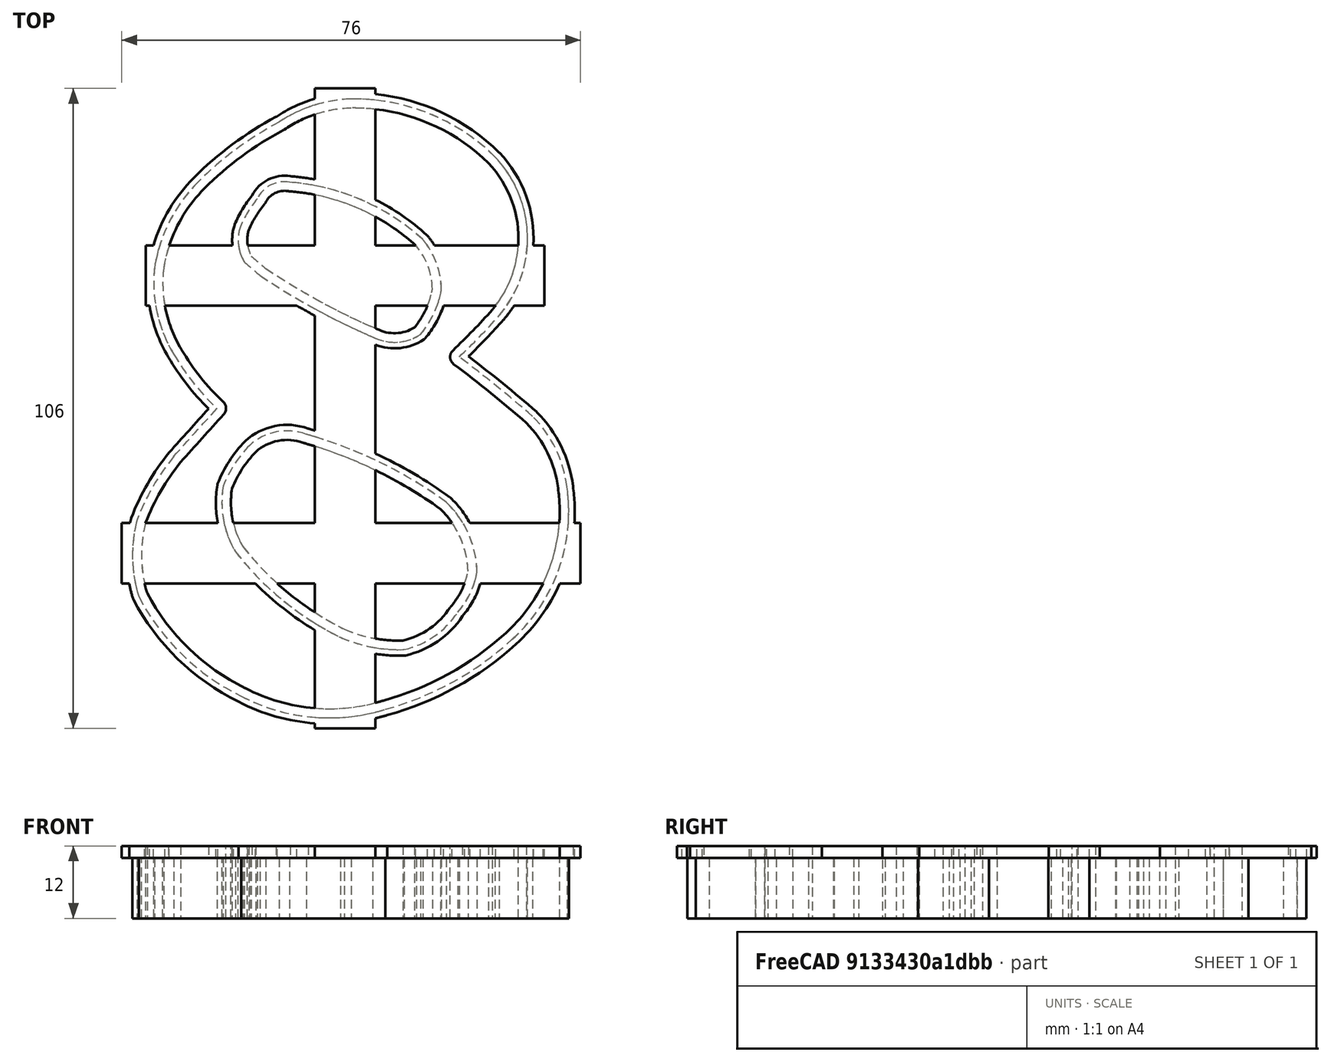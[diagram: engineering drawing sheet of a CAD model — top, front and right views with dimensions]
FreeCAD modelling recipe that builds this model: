
FCSTD DOCUMENT  (FreeCAD 0.20R27319 (Git))
Label: NumberCutter_8
License: All rights reserved
LicenseURL: http://en.wikipedia.org/wiki/All_rights_reserved
objects: Part::Box×3, Part::Offset2D×2, Part::Extrusion×2, Part::MultiFuse×2, Image::ImagePlane×1, Sketcher::SketchObject×1, PartDesign::Body×1
note: 11 computed .brp shape members not serialized (recipe doc carries the construction recipe); baked Part::Feature solids carry a one-line shape summary decoded from their .brp

FEATURE [Image::ImagePlane] ImagePlane
  XSize = 70
  YSize = 100
FEATURE [Sketcher::SketchObject] Sketch
  FullyConstrained = false
  MapMode = 5
  Support = -> [XY_Plane]
  sketch-geometry (35):
    g0: ArcOfCircle CenterX=0.459439 CenterY=17.8982 CenterZ=0 NormalX=0 NormalY=0 NormalZ=1 AngleXU=0 Radius=33.3477 StartAngle=0.793394 EndAngle=1.58457
    g1: ArcOfCircle CenterX=9.51821 CenterY=28.1344 CenterZ=0 NormalX=0 NormalY=0 NormalZ=1 AngleXU=0 Radius=19.7112 StartAngle=5.5764 EndAngle=7.03987
    g2: ArcOfCircle CenterX=-59.3435 CenterY=89.8922 CenterZ=0 NormalX=0 NormalY=0 NormalZ=1 AngleXU=0 Radius=112.205 StartAngle=5.47177 EndAngle=5.55639
    g3: ArcOfCircle CenterX=-125.981 CenterY=-181.648 CenterZ=0 NormalX=0 NormalY=0 NormalZ=1 AngleXU=0 Radius=238.464 StartAngle=0.857411 EndAngle=0.923048
    g4: ArcOfCircle CenterX=15.7711 CenterY=-15.5384 CenterZ=0 NormalX=0 NormalY=0 NormalZ=1 AngleXU=0 Radius=20.1558 StartAngle=0.124366 EndAngle=0.782145
    g5: ArcOfCircle CenterX=7.39522 CenterY=-17.0935 CenterZ=0 NormalX=0 NormalY=0 NormalZ=1 AngleXU=0 Radius=28.6643 StartAngle=5.44901 EndAngle=6.42514
    g6: ArcOfCircle CenterX=-8.01924 CenterY=-0.17697 CenterZ=0 NormalX=0 NormalY=0 NormalZ=1 AngleXU=0 Radius=51.5504 StartAngle=4.98159 EndAngle=5.45005
    g7: ArcOfCircle CenterX=-3.62856 CenterY=-19.7645 CenterZ=0 NormalX=0 NormalY=0 NormalZ=1 AngleXU=0 Radius=31.5157 StartAngle=4.23063 EndAngle=5.0126
    g8: ArcOfCircle CenterX=-1.39214 CenterY=-13.4077 CenterZ=0 NormalX=0 NormalY=0 NormalZ=1 AngleXU=0 Radius=38.1974 StartAngle=3.6262 EndAngle=4.25585
    g9: ArcOfCircle CenterX=-13.0554 CenterY=-24.3409 CenterZ=0 NormalX=0 NormalY=0 NormalZ=1 AngleXU=0 Radius=23.175 StartAngle=2.88858 EndAngle=3.44217
    g10: ArcOfCircle CenterX=0.14624 CenterY=-32.0734 CenterZ=0 NormalX=0 NormalY=0 NormalZ=1 AngleXU=0 Radius=38.1221 StartAngle=2.45634 EndAngle=2.77866
    g11: ArcOfCircle CenterX=-3185.35 CenterY=2837.49 CenterZ=0 NormalX=0 NormalY=0 NormalZ=1 AngleXU=0 Radius=4249.31 StartAngle=5.54949 EndAngle=5.552
    g12: ArcOfCircle CenterX=4.23685 CenterY=28.4724 CenterZ=0 NormalX=0 NormalY=0 NormalZ=1 AngleXU=0 Radius=38.869 StartAngle=3.66707 EndAngle=3.96361
    g13: ArcOfCircle CenterX=-9.89684 CenterY=20.8138 CenterZ=0 NormalX=0 NormalY=0 NormalZ=1 AngleXU=0 Radius=22.8052 StartAngle=3.0257 EndAngle=3.68743
    g14: ArcOfCircle CenterX=-6.96791 CenterY=19.2325 CenterZ=0 NormalX=0 NormalY=0 NormalZ=1 AngleXU=0 Radius=25.9266 StartAngle=2.36127 EndAngle=2.97816
    g15: ArcOfCircle CenterX=14.8075 CenterY=-2.80671 CenterZ=0 NormalX=0 NormalY=0 NormalZ=1 AngleXU=0 Radius=56.9079 StartAngle=2.05998 EndAngle=2.35523
    g16: ArcOfCircle CenterX=0.649489 CenterY=28.6427 CenterZ=0 NormalX=0 NormalY=0 NormalZ=1 AngleXU=0 Radius=22.6093 StartAngle=1.59953 EndAngle=2.16104
    g17: ArcOfCircle CenterX=-0.898156 CenterY=22.6525 CenterZ=0 NormalX=0 NormalY=0 NormalZ=1 AngleXU=0 Radius=18.9841 StartAngle=2.45306 EndAngle=2.73929
    g18: ArcOfCircle CenterX=-11.4978 CenterY=27.8984 CenterZ=0 NormalX=0 NormalY=0 NormalZ=1 AngleXU=0 Radius=7.20861 StartAngle=2.83333 EndAngle=3.66939
    g19: ArcOfCircle CenterX=-11.049 CenterY=32.517 CenterZ=0 NormalX=0 NormalY=0 NormalZ=1 AngleXU=0 Radius=5.01561 StartAngle=1.39646 EndAngle=2.68795
    g20: ArcOfCircle CenterX=-12.9585 CenterY=0.610782 CenterZ=0 NormalX=0 NormalY=0 NormalZ=1 AngleXU=0 Radius=36.9505 StartAngle=0.834277 EndAngle=1.4955
    g21: ArcOfCircle CenterX=1.74944 CenterY=19.4754 CenterZ=0 NormalX=0 NormalY=0 NormalZ=1 AngleXU=0 Radius=13.2157 StartAngle=0.0123752 EndAngle=0.699498
    g22: ArcOfCircle CenterX=-0.714753 CenterY=22.4724 CenterZ=0 NormalX=0 NormalY=0 NormalZ=1 AngleXU=0 Radius=15.9328 StartAngle=5.58605 EndAngle=6.1044
    g23: ArcOfCircle CenterX=7.17885 CenterY=18.7713 CenterZ=0 NormalX=0 NormalY=0 NormalZ=1 AngleXU=0 Radius=7.8291 StartAngle=4.23267 EndAngle=5.29718
    g24: ArcOfCircle CenterX=47.9675 CenterY=115.345 CenterZ=0 NormalX=0 NormalY=0 NormalZ=1 AngleXU=0 Radius=112.64 StartAngle=4.11838 EndAngle=4.3072
    g25: ArcOfCircle CenterX=164.51 CenterY=234.501 CenterZ=0 NormalX=0 NormalY=0 NormalZ=1 AngleXU=0 Radius=278.222 StartAngle=3.99821 EndAngle=4.01074
    g26: ArcOfCircle CenterX=-2.09199 CenterY=-20.4479 CenterZ=0 NormalX=0 NormalY=0 NormalZ=1 AngleXU=0 Radius=20.543 StartAngle=2.37163 EndAngle=2.76406
    g27: ArcOfCircle CenterX=-10.6158 CenterY=-12.9842 CenterZ=0 NormalX=0 NormalY=0 NormalZ=1 AngleXU=0 Radius=9.24586 StartAngle=1.21981 EndAngle=2.3094
    g28: ArcOfCircle CenterX=-27.5864 CenterY=-75.5049 CenterZ=0 NormalX=0 NormalY=0 NormalZ=1 AngleXU=0 Radius=73.999 StartAngle=0.944781 EndAngle=1.29502
    g29: ArcOfCircle CenterX=4.26387 CenterY=-27.5099 CenterZ=0 NormalX=0 NormalY=0 NormalZ=1 AngleXU=0 Radius=16.6051 StartAngle=0.0231331 EndAngle=0.805167
    g30: ArcOfCircle CenterX=-5.31205 CenterY=-15.5751 CenterZ=0 NormalX=0 NormalY=0 NormalZ=1 AngleXU=0 Radius=16.1042 StartAngle=2.97314 EndAngle=3.67342
    g31: ArcOfCircle CenterX=20.7738 CenterY=7.48175 CenterZ=0 NormalX=0 NormalY=0 NormalZ=1 AngleXU=0 Radius=50.7166 StartAngle=3.8048 EndAngle=4.25164
    g32: ArcOfCircle CenterX=7.93871 CenterY=-15.817 CenterZ=0 NormalX=0 NormalY=0 NormalZ=1 AngleXU=0 Radius=24.1675 StartAngle=4.29873 EndAngle=4.74792
    g33: ArcOfCircle CenterX=5.59944 CenterY=-25.9166 CenterZ=0 NormalX=0 NormalY=0 NormalZ=1 AngleXU=0 Radius=14.4119 StartAngle=4.93614 EndAngle=5.70292
    g34: ArcOfCircle CenterX=7.03737 CenterY=-24.6057 CenterZ=0 NormalX=0 NormalY=0 NormalZ=1 AngleXU=0 Radius=14.055 StartAngle=5.56842 EndAngle=6.10291
  constraints (38):
    c: PointOnObject(g0,g-2)
    c: Coincident(g1,g0)
    c: Coincident(g2,g1)
    c: Coincident(g3,g2)
    c: Coincident(g4,g3)
    c: Coincident(g5,g4)
    c: Coincident(g6,g5)
    c: Coincident(g7,g6)
    c: Coincident(g8,g7)
    c: Coincident(g9,g8)
    c: Coincident(g10,g9)
    c: Coincident(g11,g10)
    c: PointOnObject(g11,g-1)
    c: Coincident(g12,g11)
    c: Coincident(g13,g12)
    c: Coincident(g14,g13)
    c: Coincident(g15,g14)
    c: Coincident(g16,g15)
    c: Coincident(g16,g0)
    c: Coincident(g18,g17)
    c: Coincident(g19,g17)
    c: Coincident(g20,g19)
    c: Coincident(g21,g20)
    c: Coincident(g22,g21)
    c: Coincident(g23,g22)
    c: Coincident(g24,g23)
    c: Coincident(g25,g18)
    c: Coincident(g25,g24)
    c: Coincident(g27,g26)
    c: Coincident(g28,g27)
    c: Coincident(g28,g4)
    c: Coincident(g29,g4)
    c: Coincident(g30,g26)
    c: Coincident(g31,g30)
    c: Coincident(g32,g31)
    c: Coincident(g33,g32)
    c: Coincident(g34,g33)
    c: Coincident(g34,g29)
FEATURE [PartDesign::Body] Body  label="Number Outline"
  Group = -> [Sketch]
  Origin = -> Origin
FEATURE [Part::Offset2D] Offset2D
  Fill = true
  Intersection = false
  Join = 0
  Mode = 1
  SelfIntersection = false
  Source = -> Sketch
  Value = -1.5
FEATURE [Part::Extrusion] Extrude  label="Cutter Walls"
  Base = -> Offset2D
  Dir = (0,0,1)
  DirMode = 2
  FaceMakerClass = Part::FaceMakerBullseye
  LengthFwd = 12
  LengthRev = 0
  Reversed = true
  Solid = true
  Symmetric = false
FEATURE [Part::Box] Box  label="Support 1"
  AttacherType = Attacher::AttachEngine3D
  Height = 2
  Length = 10
  Placement = pos=(-6,-53,-2) rot=(0,0,1;0rad)
  Width = 106
FEATURE [Part::Box] Box001  label="Support 2"
  AttacherType = Attacher::AttachEngine3D
  Height = 2
  Length = 10
  Placement = pos=(38,-29,-2) rot=(0,0,1;1.5708rad)
  Width = 76
FEATURE [Part::Box] Box002  label="Support 3"
  AttacherType = Attacher::AttachEngine3D
  Height = 2
  Length = 10
  Placement = pos=(32,17,-2) rot=(0,0,1;1.5708rad)
  Width = 66
FEATURE [Part::MultiFuse] Fusion  label="Thin Wall"
  Shapes = -> [Extrude,Box,Box001,Box002]
FEATURE [Part::Offset2D] Offset2D001
  Fill = true
  Intersection = false
  Join = 0
  Mode = 1
  SelfIntersection = false
  Source = -> Sketch
  Value = 1
FEATURE [Part::Extrusion] Extrude001  label="Reinforcing"
  Base = -> Offset2D001
  Dir = (0,0,1)
  DirMode = 2
  FaceMakerClass = Part::FaceMakerBullseye
  LengthFwd = 2
  LengthRev = 0
  Reversed = true
  Solid = false
  Symmetric = false
FEATURE [Part::MultiFuse] Fusion001  label="Cutter"
  Shapes = -> [Fusion,Extrude001]
